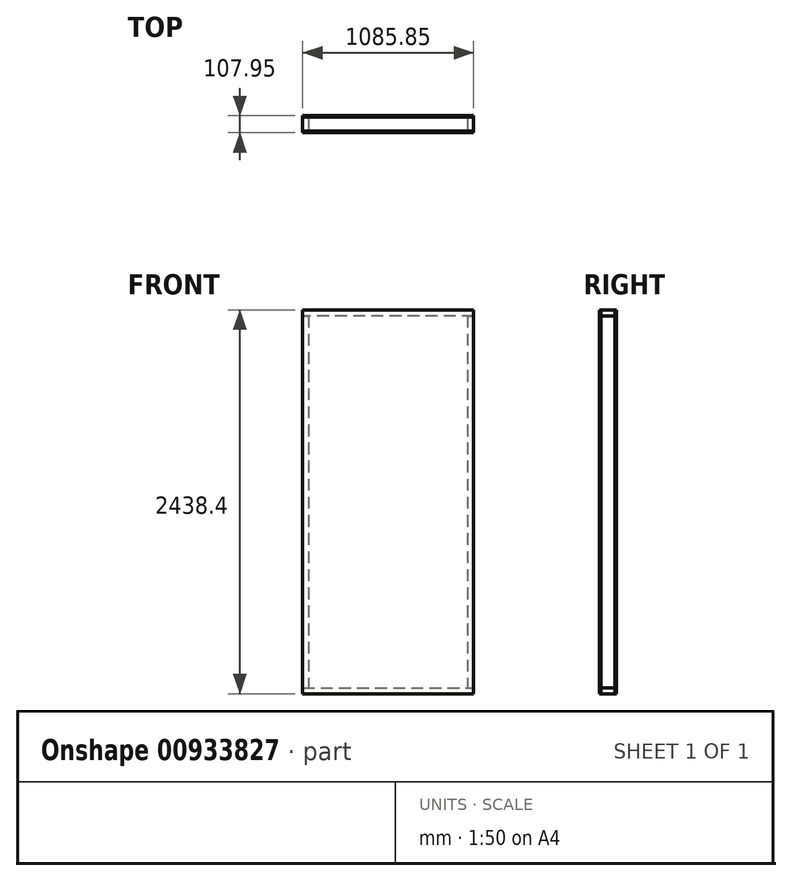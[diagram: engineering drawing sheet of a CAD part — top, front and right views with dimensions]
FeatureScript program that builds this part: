
annotation { "Feature Type Name" : "Feature", "Feature Type Description" : "" }
export const myFeature = defineFeature(function(context is Context, id is Id, definition is map)
    precondition{}
    {
        {
            var Q0;
            Q0=qCreatedBy(makeId("Top.planeOp"),FACE);
            var sketch = newSketch(context, id + "F0", { "sketchPlane" : qUnion([Q0])});
            skLineSegment(sketch, "E0.bottom", {"start": v(0, 0) * mm, "end": v(1085.85, 0) * mm});
            skLineSegment(sketch, "E0.top", {"start": v(0, -88.9) * mm, "end": v(1085.85, -88.9) * mm});
            skLineSegment(sketch, "E0.left", {"start": v(0, 0) * mm, "end": v(0, -88.9) * mm});
            skLineSegment(sketch, "E0.right", {"start": v(1085.85, 0) * mm, "end": v(1085.85, -88.9) * mm});
            skSolve(sketch);
        }
        {
            var Q0;
            Q0=makeQuery(id+"F0.imprint","IMPRINT",FACE,{"disambiguationData":[TD([[makeQuery(id+"F0.imprint","IMPRINT",EDGE,{"derivedFrom":sQuery(id+"F0.wireOp",EDGE,"E0.bottom")}),-1.0]])]});
            extrude(context, id + "F1", {"entities" : qUnion([Q0]), "depth" : 38.1 * mm, "offsetDistance" : 25.4 * mm});
        }
        {
            var Q0;
            Q0=makeQuery(id+"F1.opExtrude","CAP_FACE",FACE,{"disambiguationData":[OSD([sQuery(id+"F0.wireOp",EDGE,"E0.bottom"),sQuery(id+"F0.wireOp",EDGE,"E0.top"),sQuery(id+"F0.wireOp",EDGE,"E0.left"),sQuery(id+"F0.wireOp",EDGE,"E0.right")])],"isStart":false});
            var sketch = newSketch(context, id + "F2", { "sketchPlane" : qUnion([Q0])});
            skLineSegment(sketch, "E1.bottom", {"start": v(0, 0) * mm, "end": v(38.1, 0) * mm});
            skLineSegment(sketch, "E1.top", {"start": v(0, -88.9) * mm, "end": v(38.1, -88.9) * mm});
            skLineSegment(sketch, "E1.left", {"start": v(0, 0) * mm, "end": v(0, -88.9) * mm});
            skLineSegment(sketch, "E1.right", {"start": v(38.1, 0) * mm, "end": v(38.1, -88.9) * mm});
            skLineSegment(sketch, "E2.bottom", {"start": v(1085.85, 0) * mm, "end": v(1047.75, 0) * mm});
            skLineSegment(sketch, "E2.top", {"start": v(1085.85, -88.9) * mm, "end": v(1047.75, -88.9) * mm});
            skLineSegment(sketch, "E2.left", {"start": v(1085.85, 0) * mm, "end": v(1085.85, -88.9) * mm});
            skLineSegment(sketch, "E2.right", {"start": v(1047.75, 0) * mm, "end": v(1047.75, -88.9) * mm});
            skSolve(sketch);
        }
        {
            var Q0;
            Q0=makeQuery(id+"F2.imprint","IMPRINT",FACE,{"disambiguationData":[TD([[makeQuery(id+"F2.imprint","IMPRINT",EDGE,{"derivedFrom":sQuery(id+"F2.wireOp",EDGE,"E1.bottom")}),-1.0]])]});
            var Q1;
            Q1=makeQuery(id+"F2.imprint","IMPRINT",FACE,{"disambiguationData":[TD([[makeQuery(id+"F2.imprint","IMPRINT",EDGE,{"derivedFrom":sQuery(id+"F2.wireOp",EDGE,"E2.bottom")}),-1.0]])]});
            extrude(context, id + "F3", {"entities" : qUnion([Q0, Q1]), "depth" : 2362.2 * mm, "offsetDistance" : 25.4 * mm});
        }
        {
            var Q0;
            Q0=makeQuery(id+"F3.opExtrude","CAP_FACE",FACE,{"disambiguationData":[OSD([sQuery(id+"F2.wireOp",EDGE,"E2.bottom"),sQuery(id+"F2.wireOp",EDGE,"E2.top"),sQuery(id+"F2.wireOp",EDGE,"E2.left"),sQuery(id+"F2.wireOp",EDGE,"E2.right")])],"isStart":false});
            var sketch = newSketch(context, id + "F4", { "sketchPlane" : qUnion([Q0])});
            skLineSegment(sketch, "E3.bottom", {"start": v(1085.85, -88.9) * mm, "end": v(0, -88.9) * mm});
            skLineSegment(sketch, "E3.top", {"start": v(1085.85, 0) * mm, "end": v(0, 0) * mm});
            skLineSegment(sketch, "E3.left", {"start": v(1085.85, -88.9) * mm, "end": v(1085.85, 0) * mm});
            skLineSegment(sketch, "E3.right", {"start": v(0, -88.9) * mm, "end": v(0, 0) * mm});
            skSolve(sketch);
        }
        {
            var Q0;
            Q0 = qSketchRegion(id + "F4", true);
            extrude(context, id + "F5", {"entities" : qUnion([Q0]), "depth" : 38.1 * mm, "offsetDistance" : 25.4 * mm});
        }
        {
            var Q0;
            Q0=makeQuery(id+"F5.opExtrude","SWEPT_FACE",FACE,{"disambiguationData":[OSD([sQuery(id+"F4.wireOp",EDGE,"E3.bottom")])]});
            var sketch = newSketch(context, id + "F6", { "sketchPlane" : qUnion([Q0])});
            skLineSegment(sketch, "E4.bottom", {"start": v(1085.85, 2438.4) * mm, "end": v(0, 2438.4) * mm});
            skLineSegment(sketch, "E4.top", {"start": v(1085.85, 0) * mm, "end": v(0, 0) * mm});
            skLineSegment(sketch, "E4.left", {"start": v(1085.85, 2438.4) * mm, "end": v(1085.85, 0) * mm});
            skLineSegment(sketch, "E4.right", {"start": v(0, 2438.4) * mm, "end": v(0, 0) * mm});
            skSolve(sketch);
        }
        {
            var Q0;
            Q0 = qSketchRegion(id + "F6", true);
            extrude(context, id + "F7", {"entities" : qUnion([Q0]), "depth" : 9.52 * mm, "offsetDistance" : 25.4 * mm});
        }
        {
            var Q0;
            Q0=makeQuery(id+"F5.opExtrude","CAP_EDGE",EDGE,{"disambiguationData":[OSD([sQuery(id+"F4.wireOp",EDGE,"E3.left")])],"isStart":false});
            cPoint(context, id + "F8", {"entities" : qUnion([Q0]), "parameter" : 0.5});
        }
        {
            var Q0;
            Q0=makeQuery(id+"F3.opExtrude","CAP_EDGE",EDGE,{"disambiguationData":[OSD([sQuery(id+"F2.wireOp",EDGE,"E2.left")])],"isStart":false});
            cPoint(context, id + "F9", {"entities" : qUnion([Q0]), "parameter" : 0.5});
        }
        {
            var Q0;
            Q0=makeQuery(id+"F1.opExtrude","CAP_EDGE",EDGE,{"disambiguationData":[OSD([sQuery(id+"F0.wireOp",EDGE,"E0.left")])],"isStart":true});
            cPoint(context, id + "F10", {"entities" : qUnion([Q0]), "parameter" : 0.5});
        }
        {
            var Q0;
            Q0 = qCreatedBy(id + "F8" ,VERTEX);
            var Q1;
            Q1 = qCreatedBy(id + "F9" ,VERTEX);
            var Q2;
            Q2 = qCreatedBy(id + "F10" ,VERTEX);
            cPlane(context, id + "F11", {"entities" : qUnion([Q0, Q1, Q2]), "cplaneType" : CPlaneType.THREE_POINT, "offset" : 25.4 * mm, "width" : 152.4 * mm, "height" : 152.4 * mm});
        }
        {
            var Q0;
            Q0=makeQuery(id+"F7.opExtrude","SWEPT_BODY",BODY,{"disambiguationData":[OSD([sQuery(id+"F6.wireOp",EDGE,"E4.bottom"),sQuery(id+"F6.wireOp",EDGE,"E4.top"),sQuery(id+"F6.wireOp",EDGE,"E4.left"),sQuery(id+"F6.wireOp",EDGE,"E4.right")])]});
            var Q1;
            Q1=qCreatedBy(id+"F11.planeOp",FACE);
            mirror(context, id + "F12", {"entities" : qUnion([Q0]), "mirrorPlane" : qUnion([Q1])});
        }
    });
